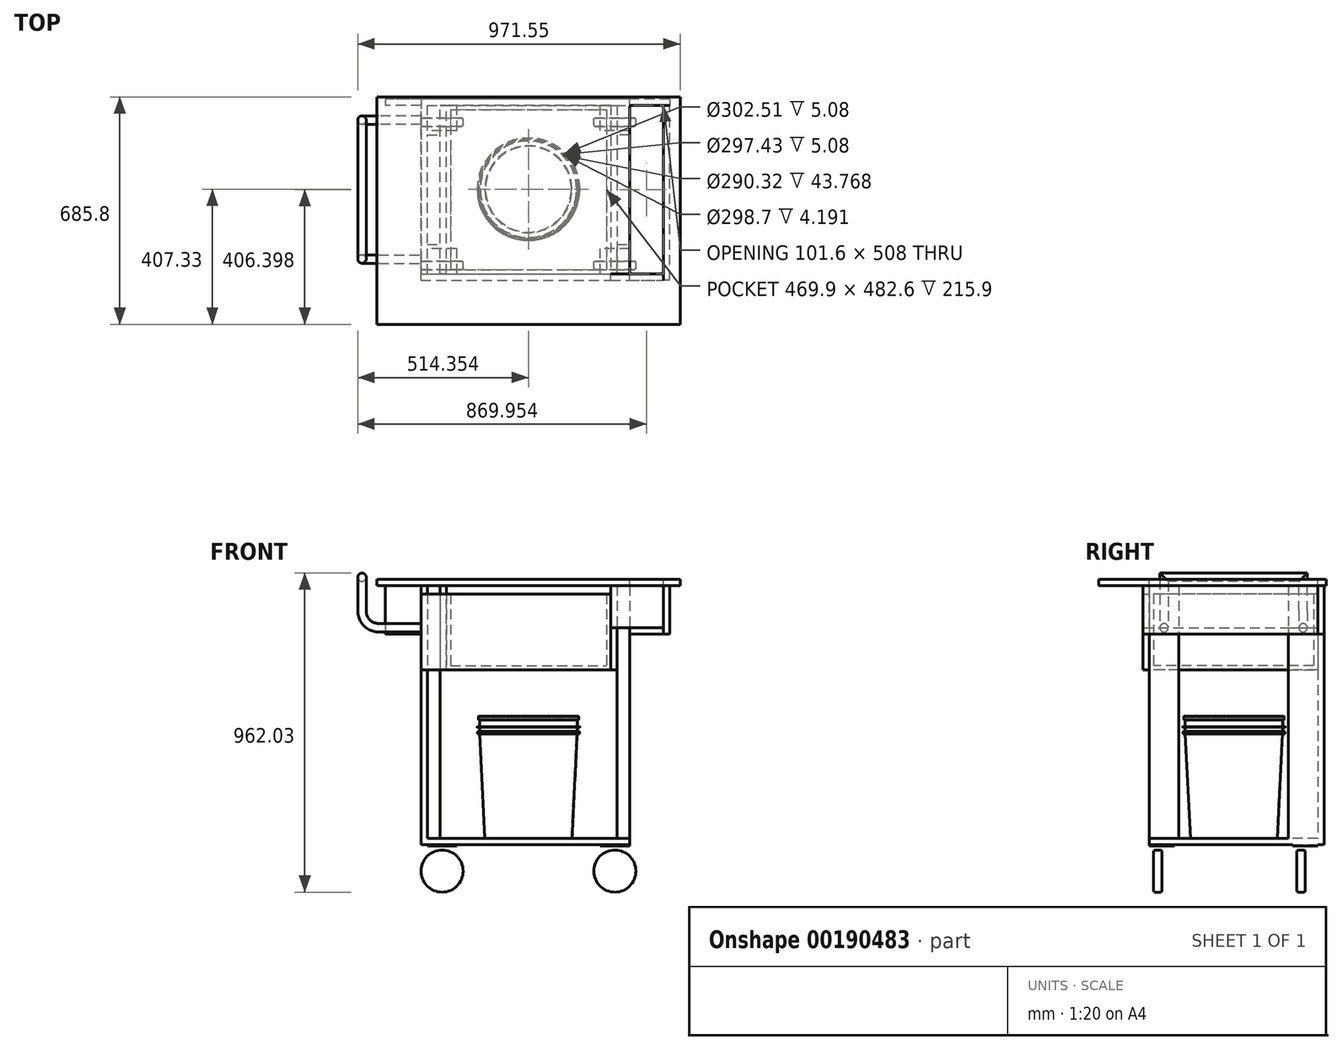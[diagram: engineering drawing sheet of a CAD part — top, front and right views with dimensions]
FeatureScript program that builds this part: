
annotation { "Feature Type Name" : "Feature", "Feature Type Description" : "" }
export const myFeature = defineFeature(function(context is Context, id is Id, definition is map)
    precondition{}
    {
        {
            var Q0;
            Q0=qCreatedBy(makeId("Top.planeOp"),FACE);
            var sketch = newSketch(context, id + "F0", { "sketchPlane" : qUnion([Q0])});
            skLineSegment(sketch, "E0.bottom", {"start": v(-54.98, -51.73) * mm, "end": v(554.62, -51.73) * mm});
            skLineSegment(sketch, "E0.top", {"start": v(-54.98, 456.27) * mm, "end": v(554.62, 456.27) * mm});
            skLineSegment(sketch, "E0.left", {"start": v(-54.98, -51.73) * mm, "end": v(-54.98, 456.27) * mm});
            skLineSegment(sketch, "E0.right", {"start": v(554.62, -51.73) * mm, "end": v(554.62, 456.27) * mm});
            skSolve(sketch);
        }
        {
            var Q0;
            Q0=makeQuery(id+"F0.imprint","IMPRINT",FACE,{"disambiguationData":[TD([[makeQuery(id+"F0.imprint","IMPRINT",EDGE,{"derivedFrom":sQuery(id+"F0.wireOp",EDGE,"E0.bottom")}),1.0]])]});
            var sketch = newSketch(context, id + "F1", { "sketchPlane" : qUnion([Q0])});
            skLineSegment(sketch, "E1.bottom", {"start": v(-54.98, 456.27) * mm, "end": v(-16.88, 456.27) * mm});
            skLineSegment(sketch, "E1.top", {"start": v(-54.98, 367.37) * mm, "end": v(-16.88, 367.37) * mm});
            skLineSegment(sketch, "E1.left", {"start": v(-54.98, 456.27) * mm, "end": v(-54.98, 367.37) * mm});
            skLineSegment(sketch, "E1.right", {"start": v(-16.88, 456.27) * mm, "end": v(-16.88, 367.37) * mm});
            skLineSegment(sketch, "E2.bottom", {"start": v(554.62, 456.27) * mm, "end": v(516.52, 456.27) * mm});
            skLineSegment(sketch, "E2.top", {"start": v(554.62, 367.37) * mm, "end": v(516.52, 367.37) * mm});
            skLineSegment(sketch, "E2.left", {"start": v(554.62, 456.27) * mm, "end": v(554.62, 367.37) * mm});
            skLineSegment(sketch, "E2.right", {"start": v(516.52, 456.27) * mm, "end": v(516.52, 367.37) * mm});
            skLineSegment(sketch, "E3.bottom", {"start": v(516.52, -51.73) * mm, "end": v(554.62, -51.73) * mm});
            skLineSegment(sketch, "E3.top", {"start": v(516.52, 37.17) * mm, "end": v(554.62, 37.17) * mm});
            skLineSegment(sketch, "E3.left", {"start": v(516.52, -51.73) * mm, "end": v(516.52, 37.17) * mm});
            skLineSegment(sketch, "E3.right", {"start": v(554.62, -51.73) * mm, "end": v(554.62, 37.17) * mm});
            skLineSegment(sketch, "E4.bottom", {"start": v(-54.98, -51.73) * mm, "end": v(-16.88, -51.73) * mm});
            skLineSegment(sketch, "E4.top", {"start": v(-54.98, 37.17) * mm, "end": v(-16.88, 37.17) * mm});
            skLineSegment(sketch, "E4.left", {"start": v(-54.98, -51.73) * mm, "end": v(-54.98, 37.17) * mm});
            skLineSegment(sketch, "E4.right", {"start": v(-16.88, -51.73) * mm, "end": v(-16.88, 37.17) * mm});
            skSolve(sketch);
        }
        {
            var Q0;
            Q0=makeQuery(id+"F1.imprint","IMPRINT",FACE,{"disambiguationData":[TD([[makeQuery(id+"F1.imprint","IMPRINT",EDGE,{"derivedFrom":sQuery(id+"F1.wireOp",EDGE,"E1.bottom")}),-1.0]])]});
            var Q1;
            Q1=makeQuery(id+"F1.imprint","IMPRINT",FACE,{"disambiguationData":[TD([[makeQuery(id+"F1.imprint","IMPRINT",EDGE,{"derivedFrom":sQuery(id+"F1.wireOp",EDGE,"E2.bottom")}),-1.0]])]});
            var Q2;
            Q2=makeQuery(id+"F1.imprint","IMPRINT",FACE,{"disambiguationData":[TD([[makeQuery(id+"F1.imprint","IMPRINT",EDGE,{"derivedFrom":sQuery(id+"F1.wireOp",EDGE,"E3.bottom")}),1.0]])]});
            var Q3;
            Q3=makeQuery(id+"F1.imprint","IMPRINT",FACE,{"disambiguationData":[TD([[makeQuery(id+"F1.imprint","IMPRINT",EDGE,{"derivedFrom":sQuery(id+"F1.wireOp",EDGE,"E4.bottom")}),1.0]])]});
            extrude(context, id + "F2", {"entities" : qUnion([Q0, Q1, Q2, Q3]), "depth" : 762 * mm});
        }
        {
            var Q0;
            Q0=makeQuery(id+"F0.imprint","IMPRINT",FACE,{"disambiguationData":[TD([[makeQuery(id+"F0.imprint","IMPRINT",EDGE,{"derivedFrom":sQuery(id+"F0.wireOp",EDGE,"E0.bottom")}),1.0]])]});
            extrude(context, id + "F3", {"entities" : qUnion([Q0]), "oppositeDirection" : true, "depth" : 19.05 * mm});
        }
        {
            var Q0;
            Q0=makeQuery(id+"F2.opExtrude","CAP_FACE",FACE,{"disambiguationData":[OSD([sQuery(id+"F1.wireOp",EDGE,"E1.bottom"),sQuery(id+"F1.wireOp",EDGE,"E1.top"),sQuery(id+"F1.wireOp",EDGE,"E1.left"),sQuery(id+"F1.wireOp",EDGE,"E1.right")])],"isStart":false});
            var sketch = newSketch(context, id + "F4", { "sketchPlane" : qUnion([Q0])});
            skLineSegment(sketch, "E5.bottom", {"start": v(-207.38, 481.67) * mm, "end": v(707.02, 481.67) * mm});
            skLineSegment(sketch, "E5.top", {"start": v(-207.38, -204.13) * mm, "end": v(707.02, -204.13) * mm});
            skLineSegment(sketch, "E5.left", {"start": v(-207.38, 481.67) * mm, "end": v(-207.38, -204.13) * mm});
            skLineSegment(sketch, "E5.right", {"start": v(707.02, 481.67) * mm, "end": v(707.02, -204.13) * mm});
            skSolve(sketch);
        }
        {
            var Q0;
            Q0=makeQuery(id+"F4.imprint","IMPRINT",FACE,{"disambiguationData":[TD([[makeQuery(id+"F4.imprint","IMPRINT",EDGE,{"derivedFrom":sQuery(id+"F4.wireOp",EDGE,"E5.top")}),1.0]])]});
            var Q1;
            Q1=makeQuery(id+"F4.imprint","IMPRINT",FACE,{"disambiguationData":[TD([[makeQuery(id+"F4.imprint","IMPRINT",EDGE,{"derivedFrom":makeQuery(id+"F2.opExtrude","CAP_EDGE",EDGE,{"disambiguationData":[OSD([sQuery(id+"F1.wireOp",EDGE,"E1.top")])],"isStart":false})}),1.0]])]});
            extrude(context, id + "F5", {"entities" : qUnion([Q0, Q1]), "depth" : 19.05 * mm});
        }
        {
            var Q0;
            Q0=qCreatedBy(makeId("Front.planeOp"),FACE);
            cPlane(context, id + "F6", {"entities" : qUnion([Q0]), "cplaneType" : CPlaneType.OFFSET, "offset" : 203.2 * mm, "oppositeDirection" : true, "width" : 152.4 * mm, "height" : 152.4 * mm});
        }
        {
            var Q0;
            Q0=qCreatedBy(id+"F6.planeOp",FACE);
            var sketch = newSketch(context, id + "F7", { "sketchPlane" : qUnion([Q0])});
            skLineSegment(sketch, "E6", {"start": v(249.82, 0) * mm, "end": v(381.02, 0) * mm});
            skLineSegment(sketch, "E7", {"start": v(249.82, 368.3) * mm, "end": v(401.08, 368.3) * mm});
            skLineSegment(sketch, "E8", {"start": v(249.82, 368.3) * mm, "end": v(249.82, 0) * mm});
            skLineSegment(sketch, "E9", {"start": v(401.08, 368.3) * mm, "end": v(401.08, 357.12) * mm});
            skLineSegment(sketch, "E10", {"start": v(401.08, 357.12) * mm, "end": v(398.54, 357.12) * mm});
            skLineSegment(sketch, "E11", {"start": v(398.54, 357.12) * mm, "end": v(398.54, 362.2) * mm});
            skLineSegment(sketch, "E12", {"start": v(398.54, 362.2) * mm, "end": v(396.9, 362.2) * mm});
            skLineSegment(sketch, "E13", {"start": v(396.9, 362.2) * mm, "end": v(396.9, 336.8) * mm});
            skLineSegment(sketch, "E14", {"start": v(396.9, 336.8) * mm, "end": v(404.51, 336.8) * mm});
            skLineSegment(sketch, "E15", {"start": v(404.51, 336.8) * mm, "end": v(404.51, 334.9) * mm});
            skLineSegment(sketch, "E16", {"start": v(404.51, 334.9) * mm, "end": v(396.9, 334.9) * mm});
            skLineSegment(sketch, "E17", {"start": v(396.9, 334.9) * mm, "end": v(396.9, 322.2) * mm});
            skLineSegment(sketch, "E18", {"start": v(396.9, 322.2) * mm, "end": v(403.37, 322.2) * mm});
            skLineSegment(sketch, "E19", {"start": v(403.37, 322.2) * mm, "end": v(403.37, 315.21) * mm});
            skLineSegment(sketch, "E20", {"start": v(403.37, 315.21) * mm, "end": v(401.08, 315.21) * mm});
            skLineSegment(sketch, "E21", {"start": v(401.08, 315.21) * mm, "end": v(401.08, 320.3) * mm});
            skLineSegment(sketch, "E22", {"start": v(401.08, 320.3) * mm, "end": v(396.9, 320.3) * mm});
            skLineSegment(sketch, "E23", {"start": v(396.9, 320.3) * mm, "end": v(381.02, 0) * mm});
            skSolve(sketch);
        }
        {
            var Q0;
            Q0=makeQuery(id+"F7.imprint","IMPRINT",FACE,{"disambiguationData":[TD([[makeQuery(id+"F7.imprint","IMPRINT",EDGE,{"derivedFrom":sQuery(id+"F7.wireOp",EDGE,"E6")}),1.0]])]});
            var Q1;
            Q1=sQuery(id+"F7.wireOp",EDGE,"E8");
            revolve(context, id + "F8", {"entities" : qUnion([Q0]), "axis" : qUnion([Q1]), "revolveType" : RevolveType.FULL});
        }
        {
            var Q0;
            Q0=makeQuery(id+"F8.opRevolve","SWEPT_FACE",FACE,{"disambiguationData":[OSD([sQuery(id+"F7.wireOp",EDGE,"E7")])]});
            shell(context, id + "F9", {"entities" : qUnion([Q0]), "thickness" : 1.9 * mm});
        }
        {
            var Q0;
            Q0=makeQuery(id+"F8.opRevolve","SWEPT_EDGE",EDGE,{"disambiguationData":[OSD([sQuery(id+"F7.wireOp",EDGE,"E18"),sQuery(id+"F7.wireOp",EDGE,"E19")])]});
            var Q1;
            Q1=makeQuery(id+"F8.opRevolve","SWEPT_EDGE",EDGE,{"disambiguationData":[OSD([sQuery(id+"F7.wireOp",EDGE,"E7"),sQuery(id+"F7.wireOp",EDGE,"E9")])]});
            fillet(context, id + "F10", {"entities" : qUnion([Q0, Q1]), "radius" : 1.52 * mm, "tangentPropagation" : true, "allowEdgeOverflow" : false});
        }
        {
            var Q0;
            Q0=makeQuery(id+"F8.opRevolve","SWEPT_EDGE",EDGE,{"disambiguationData":[OSD([sQuery(id+"F7.wireOp",EDGE,"E14"),sQuery(id+"F7.wireOp",EDGE,"E15")])]});
            var Q1;
            Q1=makeQuery(id+"F8.opRevolve","SWEPT_EDGE",EDGE,{"disambiguationData":[OSD([sQuery(id+"F7.wireOp",EDGE,"E15"),sQuery(id+"F7.wireOp",EDGE,"E16")])]});
            fillet(context, id + "F11", {"entities" : qUnion([Q0, Q1]), "radius" : 0.76 * mm, "tangentPropagation" : true, "allowEdgeOverflow" : false});
        }
        {
            var Q0;
            Q0=makeQuery(id+"F2.opExtrude","SWEPT_FACE",FACE,{"disambiguationData":[OSD([sQuery(id+"F1.wireOp",EDGE,"E2.right")])]});
            var sketch = newSketch(context, id + "F12", { "sketchPlane" : qUnion([Q0])});
            skLineSegment(sketch, "E24.bottom", {"start": v(-456.27, 762) * mm, "end": v(51.73, 762) * mm});
            skLineSegment(sketch, "E24.top", {"start": v(-456.27, 508) * mm, "end": v(51.73, 508) * mm});
            skLineSegment(sketch, "E24.left", {"start": v(-456.27, 762) * mm, "end": v(-456.27, 508) * mm});
            skLineSegment(sketch, "E24.right", {"start": v(51.73, 762) * mm, "end": v(51.73, 508) * mm});
            skSolve(sketch);
        }
        {
            var Q0;
            {var subQ3=sQuery(id+"F12.wireOp",EDGE,"E24.right");Q0=makeQuery(id+"F12.imprint","IMPRINT",FACE,{"disambiguationData":[TD([[makeQuery(id+"F12.imprint","IMPRINT",EDGE,{"derivedFrom":subQ3}),-1.0]])]});}
            var Q1;
            {var subQ0=sQuery(id+"F12.wireOp",EDGE,"E24.left");Q1=makeQuery(id+"F12.imprint","IMPRINT",FACE,{"disambiguationData":[TD([[makeQuery(id+"F12.imprint","IMPRINT",EDGE,{"derivedFrom":subQ0}),1.0]])]});}
            extrude(context, id + "F13", {"entities" : qUnion([Q0, Q1]), "depth" : 19.05 * mm});
        }
        {
            var Q0;
            Q0=makeQuery(id+"F2.opExtrude","SWEPT_FACE",FACE,{"disambiguationData":[OSD([sQuery(id+"F1.wireOp",EDGE,"E3.bottom")])]});
            var sketch = newSketch(context, id + "F14", { "sketchPlane" : qUnion([Q0])});
            skLineSegment(sketch, "E25.bottom", {"start": v(497.47, 635) * mm, "end": v(656.22, 635) * mm});
            skLineSegment(sketch, "E25.top", {"start": v(497.47, 762) * mm, "end": v(656.22, 762) * mm});
            skLineSegment(sketch, "E25.left", {"start": v(497.47, 635) * mm, "end": v(497.47, 762) * mm});
            skLineSegment(sketch, "E25.right", {"start": v(656.22, 635) * mm, "end": v(656.22, 762) * mm});
            skSolve(sketch);
        }
        {
            var Q0;
            {var subQ0=sQuery(id+"F14.wireOp",EDGE,"E25.right");Q0=makeQuery(id+"F14.imprint","IMPRINT",FACE,{"disambiguationData":[TD([[makeQuery(id+"F14.imprint","IMPRINT",EDGE,{"derivedFrom":subQ0}),1.0]])]});}
            var Q1;
            {var subQ0=sQuery(id+"F14.wireOp",EDGE,"E25.bottom");var subQ1=sQuery(id+"F1.wireOp",EDGE,"E3.bottom");var subQ4=makeQuery(id+"F2.opExtrude","SWEPT_EDGE",EDGE,{"disambiguationData":[OSD([subQ1,sQuery(id+"F1.wireOp",EDGE,"E3.right")])]});var subQ5=makeQuery(id+"F14.imprint","INTERSECT",VERTEX,{"derivedFrom":[subQ4,subQ0]});Q1=makeQuery(id+"F14.imprint","IMPRINT",FACE,{"disambiguationData":[TD([[makeQuery(id+"F14.imprint","IMPRINT",EDGE,{"disambiguationData":[TD([[subQ5,1.0]])],"derivedFrom":subQ0}),1.0]])]});}
            var Q2;
            {var subQ0=sQuery(id+"F14.wireOp",EDGE,"E25.left");Q2=makeQuery(id+"F14.imprint","IMPRINT",FACE,{"disambiguationData":[TD([[makeQuery(id+"F14.imprint","IMPRINT",EDGE,{"derivedFrom":subQ0}),-1.0]])]});}
            extrude(context, id + "F15", {"entities" : qUnion([Q0, Q1, Q2]), "depth" : 19.05 * mm});
        }
        {
            var Q0;
            Q0=makeQuery(id+"F2.opExtrude","SWEPT_FACE",FACE,{"disambiguationData":[OSD([sQuery(id+"F1.wireOp",EDGE,"E2.bottom")])]});
            var sketch = newSketch(context, id + "F16", { "sketchPlane" : qUnion([Q0])});
            skLineSegment(sketch, "E26.bottom", {"start": v(-497.47, 762) * mm, "end": v(-656.22, 762) * mm});
            skLineSegment(sketch, "E26.top", {"start": v(-497.47, 635) * mm, "end": v(-656.22, 635) * mm});
            skLineSegment(sketch, "E26.left", {"start": v(-497.47, 762) * mm, "end": v(-497.47, 635) * mm});
            skLineSegment(sketch, "E26.right", {"start": v(-656.22, 762) * mm, "end": v(-656.22, 635) * mm});
            skSolve(sketch);
        }
        {
            var Q0;
            {var subQ3=sQuery(id+"F16.wireOp",EDGE,"E26.left");Q0=makeQuery(id+"F16.imprint","IMPRINT",FACE,{"disambiguationData":[TD([[makeQuery(id+"F16.imprint","IMPRINT",EDGE,{"derivedFrom":subQ3}),-1.0]])]});}
            var Q1;
            {var subQ0=sQuery(id+"F16.wireOp",EDGE,"E26.bottom");var subQ1=sQuery(id+"F1.wireOp",EDGE,"E2.bottom");var subQ2=makeQuery(id+"F2.opExtrude","SWEPT_EDGE",EDGE,{"disambiguationData":[OSD([subQ1,sQuery(id+"F1.wireOp",EDGE,"E2.left")])]});var subQ3=makeQuery(id+"F16.imprint","INTERSECT",VERTEX,{"derivedFrom":[subQ2,subQ0]});Q1=makeQuery(id+"F16.imprint","IMPRINT",FACE,{"disambiguationData":[TD([[makeQuery(id+"F16.imprint","IMPRINT",EDGE,{"disambiguationData":[TD([[subQ3,1.0]])],"derivedFrom":subQ0}),1.0]])]});}
            var Q2;
            {var subQ3=sQuery(id+"F16.wireOp",EDGE,"E26.right");Q2=makeQuery(id+"F16.imprint","IMPRINT",FACE,{"disambiguationData":[TD([[makeQuery(id+"F16.imprint","IMPRINT",EDGE,{"derivedFrom":subQ3}),1.0]])]});}
            extrude(context, id + "F17", {"entities" : qUnion([Q0, Q1, Q2]), "depth" : 19.05 * mm});
        }
        {
            var Q0;
            Q0=makeQuery(id+"F15.opExtrude","SWEPT_FACE",FACE,{"disambiguationData":[OSD([sQuery(id+"F14.wireOp",EDGE,"E25.bottom")])]});
            var sketch = newSketch(context, id + "F18", { "sketchPlane" : qUnion([Q0])});
            skLineSegment(sketch, "E27.bottom", {"start": v(656.22, 70.78) * mm, "end": v(554.62, 70.78) * mm});
            skLineSegment(sketch, "E27.top", {"start": v(656.22, -456.27) * mm, "end": v(554.62, -456.27) * mm});
            skLineSegment(sketch, "E27.left", {"start": v(656.22, 70.78) * mm, "end": v(656.22, -456.27) * mm});
            skLineSegment(sketch, "E27.right", {"start": v(554.62, 70.78) * mm, "end": v(554.62, -456.27) * mm});
            skSolve(sketch);
        }
        {
            var Q0;
            {var subQ0=sQuery(id+"F18.wireOp",EDGE,"E27.bottom");Q0=makeQuery(id+"F18.imprint","IMPRINT",FACE,{"disambiguationData":[TD([[makeQuery(id+"F18.imprint","IMPRINT",EDGE,{"derivedFrom":subQ0}),-1.0]])]});}
            var Q1;
            {var subQ0=sQuery(id+"F18.wireOp",EDGE,"E27.top");Q1=makeQuery(id+"F18.imprint","IMPRINT",FACE,{"disambiguationData":[TD([[makeQuery(id+"F18.imprint","IMPRINT",EDGE,{"derivedFrom":subQ0}),-1.0]])]});}
            extrude(context, id + "F19", {"entities" : qUnion([Q0, Q1]), "depth" : 19.05 * mm});
        }
        {
            var Q0;
            Q0=makeQuery(id+"F15.opExtrude","SWEPT_FACE",FACE,{"disambiguationData":[OSD([sQuery(id+"F14.wireOp",EDGE,"E25.right")])]});
            var sketch = newSketch(context, id + "F20", { "sketchPlane" : qUnion([Q0])});
            skLineSegment(sketch, "E28.bottom", {"start": v(-70.78, 615.95) * mm, "end": v(456.27, 615.95) * mm});
            skLineSegment(sketch, "E28.top", {"start": v(-70.78, 762) * mm, "end": v(456.27, 762) * mm});
            skLineSegment(sketch, "E28.left", {"start": v(-70.78, 615.95) * mm, "end": v(-70.78, 762) * mm});
            skLineSegment(sketch, "E28.right", {"start": v(456.27, 615.95) * mm, "end": v(456.27, 762) * mm});
            skSolve(sketch);
        }
        {
            var Q0;
            {var subQ3=sQuery(id+"F20.wireOp",EDGE,"E28.bottom");Q0=makeQuery(id+"F20.imprint","IMPRINT",FACE,{"disambiguationData":[TD([[makeQuery(id+"F20.imprint","IMPRINT",EDGE,{"derivedFrom":subQ3}),1.0]])]});}
            var Q1;
            {var subQ1=sQuery(id+"F14.wireOp",EDGE,"E25.right");var subQ2=makeQuery(id+"F15.opExtrude","CAP_EDGE",EDGE,{"disambiguationData":[OSD([subQ1])],"isStart":true});Q1=makeQuery(id+"F20.imprint","IMPRINT",FACE,{"disambiguationData":[TD([[makeQuery(id+"F20.imprint","IMPRINT",EDGE,{"derivedFrom":subQ2}),1.0]])]});}
            extrude(context, id + "F21", {"entities" : qUnion([Q0, Q1]), "depth" : 19.05 * mm});
        }
        {
            var Q0;
            Q0=makeQuery(id+"F5.opExtrude","CAP_FACE",FACE,{"disambiguationData":[OSD([sQuery(id+"F4.wireOp",EDGE,"E5.bottom"),sQuery(id+"F4.wireOp",EDGE,"E5.top"),sQuery(id+"F4.wireOp",EDGE,"E5.left"),sQuery(id+"F4.wireOp",EDGE,"E5.right")])],"isStart":false});
            var sketch = newSketch(context, id + "F22", { "sketchPlane" : qUnion([Q0])});
            skLineSegment(sketch, "E29.bottom", {"start": v(554.62, -51.73) * mm, "end": v(656.22, -51.73) * mm});
            skLineSegment(sketch, "E29.top", {"start": v(554.62, 456.27) * mm, "end": v(656.22, 456.27) * mm});
            skLineSegment(sketch, "E29.left", {"start": v(554.62, -51.73) * mm, "end": v(554.62, 456.27) * mm});
            skLineSegment(sketch, "E29.right", {"start": v(656.22, -51.73) * mm, "end": v(656.22, 456.27) * mm});
            skSolve(sketch);
        }
        {
            var Q0;
            Q0=makeQuery(id+"F22.imprint","IMPRINT",FACE,{"disambiguationData":[TD([[makeQuery(id+"F22.imprint","IMPRINT",EDGE,{"derivedFrom":sQuery(id+"F22.wireOp",EDGE,"E29.bottom")}),1.0]])]});
            extrude(context, id + "F23", {"entities" : qUnion([Q0]), "operationType" : NewBodyOperationType.REMOVE, "oppositeDirection" : true, "depth" : 25.4 * mm});
        }
        {
            var Q0;
            Q0=makeQuery(id+"F2.opExtrude","SWEPT_FACE",FACE,{"disambiguationData":[OSD([sQuery(id+"F1.wireOp",EDGE,"E1.left")])]});
            var sketch = newSketch(context, id + "F24", { "sketchPlane" : qUnion([Q0])});
            skLineSegment(sketch, "E30.bottom", {"start": v(-456.27, 762) * mm, "end": v(51.73, 762) * mm});
            skLineSegment(sketch, "E30.top", {"start": v(-456.27, -19.05) * mm, "end": v(51.73, -19.05) * mm});
            skLineSegment(sketch, "E30.left", {"start": v(-456.27, 762) * mm, "end": v(-456.27, -19.05) * mm});
            skLineSegment(sketch, "E30.right", {"start": v(51.73, 762) * mm, "end": v(51.73, -19.05) * mm});
            skSolve(sketch);
        }
        {
            var Q0;
            {var subQ3=sQuery(id+"F1.wireOp",EDGE,"E1.left");var subQ5=makeQuery(id+"F2.opExtrude","CAP_EDGE",EDGE,{"disambiguationData":[OSD([subQ3])],"isStart":true});Q0=makeQuery(id+"F24.imprint","IMPRINT",FACE,{"disambiguationData":[TD([[makeQuery(id+"F24.imprint","IMPRINT",EDGE,{"derivedFrom":subQ5}),-1.0]])]});}
            var Q1;
            {var subQ4=sQuery(id+"F24.wireOp",EDGE,"E30.top");Q1=makeQuery(id+"F24.imprint","IMPRINT",FACE,{"disambiguationData":[TD([[makeQuery(id+"F24.imprint","IMPRINT",EDGE,{"derivedFrom":subQ4}),1.0]])]});}
            extrude(context, id + "F25", {"entities" : qUnion([Q0, Q1]), "depth" : 19.05 * mm});
        }
        {
            var Q0;
            Q0=makeQuery(id+"F3.opExtrude","CAP_FACE",FACE,{"disambiguationData":[OSD([sQuery(id+"F0.wireOp",EDGE,"E0.bottom"),sQuery(id+"F0.wireOp",EDGE,"E0.top"),sQuery(id+"F0.wireOp",EDGE,"E0.left"),sQuery(id+"F0.wireOp",EDGE,"E0.right")])],"isStart":false});
            var sketch = newSketch(context, id + "F26", { "sketchPlane" : qUnion([Q0])});
            skLineSegment(sketch, "E31.bottom", {"start": v(554.62, 51.73) * mm, "end": v(465.72, 51.73) * mm});
            skLineSegment(sketch, "E31.top", {"start": v(554.62, -24.47) * mm, "end": v(465.72, -24.47) * mm});
            skLineSegment(sketch, "E31.left", {"start": v(554.62, 51.73) * mm, "end": v(554.62, -24.47) * mm});
            skLineSegment(sketch, "E31.right", {"start": v(465.72, 51.73) * mm, "end": v(465.72, -24.47) * mm});
            skLineSegment(sketch, "E32.0.1.0", {"start": v(554.62, -380.07) * mm, "end": v(554.62, -456.27) * mm});
            skLineSegment(sketch, "E32.0.1.1", {"start": v(554.62, -456.27) * mm, "end": v(465.72, -456.27) * mm});
            skLineSegment(sketch, "E32.0.1.2", {"start": v(465.72, -380.07) * mm, "end": v(465.72, -456.27) * mm});
            skLineSegment(sketch, "E32.0.1.3", {"start": v(554.62, -380.07) * mm, "end": v(465.72, -380.07) * mm});
            skLineSegment(sketch, "E32.1.0.0", {"start": v(33.92, 51.73) * mm, "end": v(33.92, -24.47) * mm});
            skLineSegment(sketch, "E32.1.0.1", {"start": v(33.92, -24.47) * mm, "end": v(-54.98, -24.47) * mm});
            skLineSegment(sketch, "E32.1.0.2", {"start": v(-54.98, 51.73) * mm, "end": v(-54.98, -24.47) * mm});
            skLineSegment(sketch, "E32.1.0.3", {"start": v(33.92, 51.73) * mm, "end": v(-54.98, 51.73) * mm});
            skLineSegment(sketch, "E32.1.1.0", {"start": v(33.92, -380.07) * mm, "end": v(33.92, -456.27) * mm});
            skLineSegment(sketch, "E32.1.1.1", {"start": v(33.92, -456.27) * mm, "end": v(-54.98, -456.27) * mm});
            skLineSegment(sketch, "E32.1.1.2", {"start": v(-54.98, -380.07) * mm, "end": v(-54.98, -456.27) * mm});
            skLineSegment(sketch, "E32.1.1.3", {"start": v(33.92, -380.07) * mm, "end": v(-54.98, -380.07) * mm});
            skLineSegment(sketch, "E32.direction1", {"start": v(554.62, -24.47) * mm, "end": v(33.92, -24.47) * mm, "construction": true});
            skLineSegment(sketch, "E32.direction2", {"start": v(554.62, -24.47) * mm, "end": v(554.62, -456.27) * mm, "construction": true});
            skSolve(sketch);
        }
        {
            var Q0;
            Q0=makeQuery(id+"F26.imprint","IMPRINT",FACE,{"disambiguationData":[TD([[makeQuery(id+"F26.imprint","IMPRINT",EDGE,{"derivedFrom":sQuery(id+"F26.wireOp",EDGE,"E31.bottom")}),-1.0]])]});
            var Q1;
            Q1=makeQuery(id+"F26.imprint","IMPRINT",FACE,{"disambiguationData":[TD([[makeQuery(id+"F26.imprint","IMPRINT",EDGE,{"derivedFrom":sQuery(id+"F26.wireOp",EDGE,"E32.0.1.0")}),-1.0]])]});
            var Q2;
            Q2=makeQuery(id+"F26.imprint","IMPRINT",FACE,{"disambiguationData":[TD([[makeQuery(id+"F26.imprint","IMPRINT",EDGE,{"derivedFrom":sQuery(id+"F26.wireOp",EDGE,"E32.1.1.0")}),-1.0]])]});
            var Q3;
            Q3=makeQuery(id+"F26.imprint","IMPRINT",FACE,{"disambiguationData":[TD([[makeQuery(id+"F26.imprint","IMPRINT",EDGE,{"derivedFrom":sQuery(id+"F26.wireOp",EDGE,"E32.1.0.0")}),-1.0]])]});
            extrude(context, id + "F27", {"entities" : qUnion([Q0, Q1, Q2, Q3]), "depth" : 3.17 * mm});
        }
        {
            var Q0;
            Q0=makeQuery(id+"F3.opExtrude","SWEPT_FACE",FACE,{"disambiguationData":[OSD([sQuery(id+"F0.wireOp",EDGE,"E0.bottom")])]});
            cPlane(context, id + "F28", {"entities" : qUnion([Q0]), "cplaneType" : CPlaneType.OFFSET, "offset" : 38.1 * mm, "oppositeDirection" : true, "width" : 152.4 * mm, "height" : 152.4 * mm});
        }
        {
            var Q0;
            Q0=qCreatedBy(id+"F28.planeOp",FACE);
            var sketch = newSketch(context, id + "F29", { "sketchPlane" : qUnion([Q0])});
            skCircle(sketch, "E33", {"center": v(510.17, -98.43) * mm, "radius": 63.5 * mm});
            skCircle(sketch, "E34.1.0.0", {"center": v(-10.53, -98.43) * mm, "radius": 63.5 * mm});
            skLineSegment(sketch, "E34.direction1", {"start": v(510.17, -98.43) * mm, "end": v(-10.53, -98.43) * mm, "construction": true});
            skSolve(sketch);
        }
        {
            var Q0;
            Q0=makeQuery(id+"F2.opExtrude","SWEPT_FACE",FACE,{"disambiguationData":[OSD([sQuery(id+"F1.wireOp",EDGE,"E2.bottom")])]});
            cPlane(context, id + "F30", {"entities" : qUnion([Q0]), "cplaneType" : CPlaneType.OFFSET, "offset" : 38.1 * mm, "oppositeDirection" : true, "width" : 152.4 * mm, "height" : 152.4 * mm});
        }
        {
            var Q0;
            Q0=qCreatedBy(id+"F30.planeOp",FACE);
            var sketch = newSketch(context, id + "F31", { "sketchPlane" : qUnion([Q0])});
            skCircle(sketch, "E35", {"center": v(-510.17, -98.43) * mm, "radius": 63.5 * mm});
            skCircle(sketch, "E36", {"center": v(10.53, -98.42) * mm, "radius": 63.5 * mm});
            skSolve(sketch);
        }
        {
            var Q0;
            Q0=makeQuery(id+"F29.imprint","IMPRINT",FACE,{"disambiguationData":[TD([[makeQuery(id+"F29.imprint","IMPRINT",EDGE,{"derivedFrom":sQuery(id+"F29.wireOp",EDGE,"E33")}),1.0]])]});
            var Q1;
            Q1=makeQuery(id+"F31.imprint","IMPRINT",FACE,{"disambiguationData":[TD([[makeQuery(id+"F31.imprint","IMPRINT",EDGE,{"derivedFrom":sQuery(id+"F31.wireOp",EDGE,"E35")}),1.0]])]});
            var Q2;
            Q2=makeQuery(id+"F29.imprint","IMPRINT",FACE,{"disambiguationData":[TD([[makeQuery(id+"F29.imprint","IMPRINT",EDGE,{"derivedFrom":sQuery(id+"F29.wireOp",EDGE,"E34.1.0.0")}),1.0]])]});
            var Q3;
            Q3=makeQuery(id+"F31.imprint","IMPRINT",FACE,{"disambiguationData":[TD([[makeQuery(id+"F31.imprint","IMPRINT",EDGE,{"derivedFrom":sQuery(id+"F31.wireOp",EDGE,"E36")}),1.0]])]});
            extrude(context, id + "F32", {"entities" : qUnion([Q0, Q1, Q2, Q3]), "depth" : 25.4 * mm});
        }
        {
            var Q0;
            Q0=makeQuery(id+"F32.opExtrude","CAP_EDGE",EDGE,{"disambiguationData":[OSD([sQuery(id+"F29.wireOp",EDGE,"E34.1.0.0")])],"isStart":true});
            var Q1;
            Q1=makeQuery(id+"F32.opExtrude","CAP_EDGE",EDGE,{"disambiguationData":[OSD([sQuery(id+"F29.wireOp",EDGE,"E34.1.0.0")])],"isStart":false});
            var Q2;
            Q2=makeQuery(id+"F32.opExtrude","CAP_EDGE",EDGE,{"disambiguationData":[OSD([sQuery(id+"F31.wireOp",EDGE,"E36")])],"isStart":false});
            var Q3;
            Q3=makeQuery(id+"F32.opExtrude","CAP_EDGE",EDGE,{"disambiguationData":[OSD([sQuery(id+"F31.wireOp",EDGE,"E36")])],"isStart":true});
            var Q4;
            Q4=makeQuery(id+"F32.opExtrude","CAP_EDGE",EDGE,{"disambiguationData":[OSD([sQuery(id+"F29.wireOp",EDGE,"E33")])],"isStart":false});
            var Q5;
            Q5=makeQuery(id+"F32.opExtrude","CAP_EDGE",EDGE,{"disambiguationData":[OSD([sQuery(id+"F29.wireOp",EDGE,"E33")])],"isStart":true});
            var Q6;
            Q6=makeQuery(id+"F32.opExtrude","CAP_EDGE",EDGE,{"disambiguationData":[OSD([sQuery(id+"F31.wireOp",EDGE,"E35")])],"isStart":false});
            var Q7;
            Q7=makeQuery(id+"F32.opExtrude","CAP_EDGE",EDGE,{"disambiguationData":[OSD([sQuery(id+"F31.wireOp",EDGE,"E35")])],"isStart":true});
            fillet(context, id + "F33", {"entities" : qUnion([Q0, Q1, Q2, Q3, Q4, Q5, Q6, Q7]), "radius" : 5.08 * mm, "tangentPropagation" : true, "allowEdgeOverflow" : false});
        }
        {
            var Q0;
            Q0=makeQuery(id+"F2.opExtrude","SWEPT_FACE",FACE,{"disambiguationData":[OSD([sQuery(id+"F1.wireOp",EDGE,"E4.right")])]});
            var sketch = newSketch(context, id + "F34", { "sketchPlane" : qUnion([Q0])});
            skLineSegment(sketch, "E37.bottom", {"start": v(-51.73, 508) * mm, "end": v(456.27, 508) * mm});
            skLineSegment(sketch, "E37.top", {"start": v(-51.73, 762) * mm, "end": v(456.27, 762) * mm});
            skLineSegment(sketch, "E37.left", {"start": v(-51.73, 508) * mm, "end": v(-51.73, 762) * mm});
            skLineSegment(sketch, "E37.right", {"start": v(456.27, 508) * mm, "end": v(456.27, 762) * mm});
            skSolve(sketch);
        }
        {
            var Q0;
            {var subQ0=sQuery(id+"F34.wireOp",EDGE,"E37.left");Q0=makeQuery(id+"F34.imprint","IMPRINT",FACE,{"disambiguationData":[TD([[makeQuery(id+"F34.imprint","IMPRINT",EDGE,{"derivedFrom":subQ0}),1.0]])]});}
            var Q1;
            {var subQ0=sQuery(id+"F34.wireOp",EDGE,"E37.right");Q1=makeQuery(id+"F34.imprint","IMPRINT",FACE,{"disambiguationData":[TD([[makeQuery(id+"F34.imprint","IMPRINT",EDGE,{"derivedFrom":subQ0}),1.0]])]});}
            extrude(context, id + "F35", {"entities" : qUnion([Q0, Q1]), "depth" : 19.05 * mm});
        }
        {
            var Q0;
            Q0=makeQuery(id+"F17.opExtrude","SWEPT_BODY",BODY,{"disambiguationData":[OSD([sQuery(id+"F16.wireOp",EDGE,"E26.bottom"),sQuery(id+"F16.wireOp",EDGE,"E26.top"),sQuery(id+"F16.wireOp",EDGE,"E26.left"),sQuery(id+"F16.wireOp",EDGE,"E26.right")])]});
            deleteBodies(context, id + "F36", {"entities" : qUnion([Q0])});
        }
        {
            var Q0;
            Q0=makeQuery(id+"F2.opExtrude","SWEPT_FACE",FACE,{"disambiguationData":[OSD([sQuery(id+"F1.wireOp",EDGE,"E2.bottom")])]});
            var sketch = newSketch(context, id + "F37", { "sketchPlane" : qUnion([Q0])});
            skLineSegment(sketch, "E38.bottom", {"start": v(-675.27, 762) * mm, "end": v(181.98, 762) * mm});
            skLineSegment(sketch, "E38.top", {"start": v(-675.27, 615.95) * mm, "end": v(181.98, 615.95) * mm});
            skLineSegment(sketch, "E38.left", {"start": v(-675.27, 762) * mm, "end": v(-675.27, 615.95) * mm});
            skLineSegment(sketch, "E38.right", {"start": v(181.98, 762) * mm, "end": v(181.98, 615.95) * mm});
            skSolve(sketch);
        }
        {
            var Q0;
            {var subQ1=sQuery(id+"F1.wireOp",EDGE,"E2.bottom");var subQ6=makeQuery(id+"F2.opExtrude","CAP_EDGE",EDGE,{"disambiguationData":[OSD([subQ1])],"isStart":true});Q0=makeQuery(id+"F37.imprint","IMPRINT",FACE,{"disambiguationData":[TD([[makeQuery(id+"F37.imprint","IMPRINT",EDGE,{"derivedFrom":subQ6}),-1.0]])]});}
            var sketch = newSketch(context, id + "F38", { "sketchPlane" : qUnion([Q0])});
            skLineSegment(sketch, "E39.bottom", {"start": v(-554.62, 615.95) * mm, "end": v(74.03, 615.95) * mm});
            skLineSegment(sketch, "E39.top", {"start": v(-554.62, -19.05) * mm, "end": v(74.03, -19.05) * mm});
            skLineSegment(sketch, "E39.left", {"start": v(-554.62, 615.95) * mm, "end": v(-554.62, -19.05) * mm});
            skLineSegment(sketch, "E39.right", {"start": v(74.03, 615.95) * mm, "end": v(74.03, -19.05) * mm});
            skSolve(sketch);
        }
        {
            var Q0;
            {var subQ3=sQuery(id+"F37.wireOp",EDGE,"E38.right");Q0=makeQuery(id+"F37.imprint","IMPRINT",FACE,{"disambiguationData":[TD([[makeQuery(id+"F37.imprint","IMPRINT",EDGE,{"derivedFrom":subQ3}),-1.0]])]});}
            var Q1;
            {var subQ0=sQuery(id+"F37.wireOp",EDGE,"E38.bottom");var subQ1=sQuery(id+"F1.wireOp",EDGE,"E2.bottom");var subQ2=makeQuery(id+"F2.opExtrude","SWEPT_EDGE",EDGE,{"disambiguationData":[OSD([subQ1,sQuery(id+"F1.wireOp",EDGE,"E2.left")])]});var subQ3=makeQuery(id+"F37.imprint","INTERSECT",VERTEX,{"derivedFrom":[subQ2,subQ0]});var subQ4=makeQuery(id+"F2.opExtrude","SWEPT_EDGE",EDGE,{"disambiguationData":[OSD([sQuery(id+"F0.wireOp",EDGE,"E0.top"),subQ1,sQuery(id+"F1.wireOp",EDGE,"E2.right")])]});var subQ5=makeQuery(id+"F37.imprint","INTERSECT",VERTEX,{"derivedFrom":[subQ4,subQ0]});Q1=makeQuery(id+"F37.imprint","IMPRINT",FACE,{"disambiguationData":[TD([[makeQuery(id+"F37.imprint","IMPRINT",EDGE,{"disambiguationData":[TD([[subQ3,1.0],[subQ5,-1.0]])],"derivedFrom":subQ0}),1.0]])]});}
            var Q2;
            {var subQ3=sQuery(id+"F37.wireOp",EDGE,"E38.left");Q2=makeQuery(id+"F37.imprint","IMPRINT",FACE,{"disambiguationData":[TD([[makeQuery(id+"F37.imprint","IMPRINT",EDGE,{"derivedFrom":subQ3}),1.0]])]});}
            extrude(context, id + "F39", {"entities" : qUnion([Q0, Q1, Q2]), "depth" : 19.05 * mm});
        }
        {
            var Q0;
            {var subQ3=sQuery(id+"F1.wireOp",EDGE,"E2.bottom");var subQ4=makeQuery(id+"F2.opExtrude","CAP_EDGE",EDGE,{"disambiguationData":[OSD([subQ3])],"isStart":true});var subQ7=makeQuery(id+"F37.imprint","IMPRINT",EDGE,{"derivedFrom":subQ4});Q0=makeQuery(id+"F38.imprint","IMPRINT",FACE,{"disambiguationData":[TD([[makeQuery(id+"F38.imprint","IMPRINT",EDGE,{"derivedFrom":subQ7}),-1.0]])]});}
            var Q1;
            {var subQ4=sQuery(id+"F38.wireOp",EDGE,"E39.top");Q1=makeQuery(id+"F38.imprint","IMPRINT",FACE,{"disambiguationData":[TD([[makeQuery(id+"F38.imprint","IMPRINT",EDGE,{"derivedFrom":subQ4}),1.0]])]});}
            extrude(context, id + "F40", {"entities" : qUnion([Q0, Q1]), "operationType" : NewBodyOperationType.ADD, "depth" : 19.05 * mm});
        }
        {
            var Q0;
            Q0=makeQuery(id+"F23.boolean.opBoolean","COPY",EDGE,{"derivedFrom":makeQuery(id+"F23.opExtrude","SWEPT_EDGE",EDGE,{"disambiguationData":[OSD([sQuery(id+"F22.wireOp",EDGE,"E29.bottom"),sQuery(id+"F22.wireOp",EDGE,"E29.left")])]})});
            var Q1;
            Q1=makeQuery(id+"F23.boolean.opBoolean","COPY",EDGE,{"derivedFrom":makeQuery(id+"F23.opExtrude","SWEPT_EDGE",EDGE,{"disambiguationData":[OSD([sQuery(id+"F22.wireOp",EDGE,"E29.bottom"),sQuery(id+"F22.wireOp",EDGE,"E29.right")])]})});
            var Q2;
            Q2=makeQuery(id+"F23.boolean.opBoolean","COPY",EDGE,{"derivedFrom":makeQuery(id+"F23.opExtrude","SWEPT_EDGE",EDGE,{"disambiguationData":[OSD([sQuery(id+"F22.wireOp",EDGE,"E29.top"),sQuery(id+"F22.wireOp",EDGE,"E29.right")])]})});
            var Q3;
            Q3=makeQuery(id+"F23.boolean.opBoolean","COPY",EDGE,{"derivedFrom":makeQuery(id+"F23.opExtrude","SWEPT_EDGE",EDGE,{"disambiguationData":[OSD([sQuery(id+"F22.wireOp",EDGE,"E29.top"),sQuery(id+"F22.wireOp",EDGE,"E29.left")])]})});
            fillet(context, id + "F41", {"entities" : qUnion([Q0, Q1, Q2, Q3]), "radius" : 6.35 * mm, "tangentPropagation" : true, "allowEdgeOverflow" : false});
        }
        {
            var Q0;
            Q0=makeQuery(id+"F2.opExtrude","SWEPT_FACE",FACE,{"disambiguationData":[OSD([sQuery(id+"F1.wireOp",EDGE,"E4.bottom")])]});
            cPlane(context, id + "F42", {"entities" : qUnion([Q0]), "cplaneType" : CPlaneType.OFFSET, "offset" : 44.45 * mm, "oppositeDirection" : true, "width" : 152.4 * mm, "height" : 152.4 * mm});
        }
        {
            var Q0;
            Q0=qCreatedBy(id+"F42.planeOp",FACE);
            var sketch = newSketch(context, id + "F43", { "sketchPlane" : qUnion([Q0])});
            skLineSegment(sketch, "E40", {"start": v(-74.03, 635) * mm, "end": v(-201.03, 635) * mm});
            skLineSegment(sketch, "E41", {"start": v(-251.83, 685.8) * mm, "end": v(-251.83, 787.4) * mm});
            skPoint(sketch, "E42.visualSharp", {"position": v(-251.83, 635) * mm});
            skArc(sketch, "E42.filletArc", {"start": v(-251.83, 685.8) * mm, "mid": v(-236.95, 649.88) * mm, "end": v(-201.03, 635) * mm});
            skSolve(sketch);
        }
        {
            var Q0;
            Q0=makeQuery(id+"F40.boolean.opBoolean","MERGE",FACE,{"derivedFrom":[makeQuery(id+"F39.opExtrude","CAP_FACE",FACE,{"disambiguationData":[OSD([sQuery(id+"F37.wireOp",EDGE,"E38.bottom"),sQuery(id+"F37.wireOp",EDGE,"E38.top"),sQuery(id+"F37.wireOp",EDGE,"E38.left"),sQuery(id+"F37.wireOp",EDGE,"E38.right")])],"isStart":false}),makeQuery(id+"F40.opExtrude","CAP_FACE",FACE,{"disambiguationData":[OSD([sQuery(id+"F38.wireOp",EDGE,"E39.bottom"),sQuery(id+"F38.wireOp",EDGE,"E39.top"),sQuery(id+"F38.wireOp",EDGE,"E39.left"),sQuery(id+"F38.wireOp",EDGE,"E39.right")])],"isStart":false})]});
            cPlane(context, id + "F44", {"entities" : qUnion([Q0]), "cplaneType" : CPlaneType.OFFSET, "offset" : 63.5 * mm, "oppositeDirection" : true, "width" : 152.4 * mm, "height" : 152.4 * mm});
        }
        {
            var Q0;
            Q0=qCreatedBy(id+"F44.planeOp",FACE);
            var sketch = newSketch(context, id + "F45", { "sketchPlane" : qUnion([Q0])});
            skLineSegment(sketch, "E43", {"start": v(74.03, 635) * mm, "end": v(201.03, 635) * mm});
            skLineSegment(sketch, "E44", {"start": v(251.83, 685.8) * mm, "end": v(251.83, 787.4) * mm});
            skPoint(sketch, "E45.visualSharp", {"position": v(251.83, 635) * mm});
            skArc(sketch, "E45.filletArc", {"start": v(201.03, 635) * mm, "mid": v(236.95, 649.88) * mm, "end": v(251.83, 685.8) * mm});
            skSolve(sketch);
        }
        {
            var Q0;
            Q0=sQuery(id+"F45.wireOp",VERTEX,"E44.end");
            var Q1;
            Q1=sQuery(id+"F45.wireOp",VERTEX,"E45.filletArc.end");
            var Q2;
            Q2=sQuery(id+"F43.wireOp",VERTEX,"E42.filletArc.start");
            cPlane(context, id + "F46", {"entities" : qUnion([Q0, Q1, Q2]), "cplaneType" : CPlaneType.THREE_POINT, "offset" : 25.4 * mm, "width" : 152.4 * mm, "height" : 152.4 * mm});
        }
        {
            var Q0;
            Q0=makeQuery(id+"F25.opExtrude","CAP_FACE",FACE,{"disambiguationData":[OSD([sQuery(id+"F24.wireOp",EDGE,"E30.bottom"),sQuery(id+"F24.wireOp",EDGE,"E30.top"),sQuery(id+"F24.wireOp",EDGE,"E30.left"),sQuery(id+"F24.wireOp",EDGE,"E30.right")])],"isStart":false});
            var sketch = newSketch(context, id + "F47", { "sketchPlane" : qUnion([Q0])});
            skCircle(sketch, "E46", {"center": v(-411.82, 635) * mm, "radius": 12.7 * mm});
            skSolve(sketch);
        }
        {
            var Q0;
            Q0=qCreatedBy(id+"F46.planeOp",FACE);
            var sketch = newSketch(context, id + "F48", { "sketchPlane" : qUnion([Q0])});
            skLineSegment(sketch, "E47", {"start": v(411.82, 787.4) * mm, "end": v(-7.28, 787.4) * mm});
            skSolve(sketch);
        }
        {
            var Q0;
            Q0=makeQuery(id+"F47.imprint","IMPRINT",FACE,{"disambiguationData":[TD([[makeQuery(id+"F47.imprint","IMPRINT",EDGE,{"derivedFrom":sQuery(id+"F47.wireOp",EDGE,"E46")}),1.0]])]});
            var Q1;
            Q1=sQuery(id+"F45.wireOp",EDGE,"E43");
            var Q2;
            Q2=sQuery(id+"F45.wireOp",EDGE,"E45.filletArc");
            var Q3;
            Q3=sQuery(id+"F45.wireOp",EDGE,"E44");
            var Q4;
            Q4=sQuery(id+"F48.wireOp",EDGE,"E47");
            var Q5;
            Q5=sQuery(id+"F43.wireOp",EDGE,"E41");
            var Q6;
            Q6=sQuery(id+"F43.wireOp",EDGE,"E42.filletArc");
            var Q7;
            Q7=sQuery(id+"F43.wireOp",EDGE,"E40");
            sweep(context, id + "F49", {"profiles" : qUnion([Q0]), "path" : qUnion([Q1, Q2, Q3, Q4, Q5, Q6, Q7])});
        }
        {
            var Q0;
            Q0=makeQuery(id+"F35.opExtrude","SWEPT_FACE",FACE,{"disambiguationData":[OSD([sQuery(id+"F34.wireOp",EDGE,"E37.left")])]});
            var sketch = newSketch(context, id + "F50", { "sketchPlane" : qUnion([Q0])});
            skLineSegment(sketch, "E48.bottom", {"start": v(2.17, 736.6) * mm, "end": v(497.47, 736.6) * mm});
            skLineSegment(sketch, "E48.top", {"start": v(2.17, 508) * mm, "end": v(497.47, 508) * mm});
            skLineSegment(sketch, "E48.left", {"start": v(2.17, 736.6) * mm, "end": v(2.17, 508) * mm});
            skLineSegment(sketch, "E48.right", {"start": v(497.47, 736.6) * mm, "end": v(497.47, 508) * mm});
            skSolve(sketch);
        }
        {
            var Q0;
            Q0=makeQuery(id+"F50.imprint","IMPRINT",FACE,{"disambiguationData":[TD([[makeQuery(id+"F50.imprint","IMPRINT",EDGE,{"derivedFrom":sQuery(id+"F50.wireOp",EDGE,"E48.bottom")}),-1.0]])]});
            var Q1;
            Q1=makeQuery(id+"F40.boolean.opBoolean","MERGE",FACE,{"derivedFrom":[makeQuery(id+"F39.opExtrude","CAP_FACE",FACE,{"disambiguationData":[OSD([sQuery(id+"F37.wireOp",EDGE,"E38.bottom"),sQuery(id+"F37.wireOp",EDGE,"E38.top"),sQuery(id+"F37.wireOp",EDGE,"E38.left"),sQuery(id+"F37.wireOp",EDGE,"E38.right")])],"isStart":true}),makeQuery(id+"F40.opExtrude","CAP_FACE",FACE,{"disambiguationData":[OSD([sQuery(id+"F38.wireOp",EDGE,"E39.bottom"),sQuery(id+"F38.wireOp",EDGE,"E39.top"),sQuery(id+"F38.wireOp",EDGE,"E39.left"),sQuery(id+"F38.wireOp",EDGE,"E39.right")])],"isStart":true})]});
            extrude(context, id + "F51", {"entities" : qUnion([Q0]), "endBound" : BoundingType.UP_TO_SURFACE, "oppositeDirection" : true, "endBoundEntityFace" : qUnion([Q1]), "depth" : 25.4 * mm});
        }
        {
            var Q0;
            Q0=makeQuery(id+"F51.opExtrude","SWEPT_FACE",FACE,{"disambiguationData":[OSD([sQuery(id+"F50.wireOp",EDGE,"E48.bottom")])]});
            shell(context, id + "F52", {"entities" : qUnion([Q0]), "thickness" : 12.7 * mm});
        }
        {
            var Q0;
            Q0=makeQuery(id+"F51.opExtrude","CAP_FACE",FACE,{"disambiguationData":[OSD([sQuery(id+"F50.wireOp",EDGE,"E48.bottom"),sQuery(id+"F50.wireOp",EDGE,"E48.top"),sQuery(id+"F50.wireOp",EDGE,"E48.left"),sQuery(id+"F50.wireOp",EDGE,"E48.right")])],"isStart":true});
            var sketch = newSketch(context, id + "F53", { "sketchPlane" : qUnion([Q0])});
            skLineSegment(sketch, "E49.bottom", {"start": v(-74.03, 736.6) * mm, "end": v(497.47, 736.6) * mm});
            skLineSegment(sketch, "E49.top", {"start": v(-74.03, 508) * mm, "end": v(497.47, 508) * mm});
            skLineSegment(sketch, "E49.left", {"start": v(-74.03, 736.6) * mm, "end": v(-74.03, 508) * mm});
            skLineSegment(sketch, "E49.right", {"start": v(497.47, 736.6) * mm, "end": v(497.47, 508) * mm});
            skSolve(sketch);
        }
        {
            var Q0;
            {var subQ2=sQuery(id+"F53.wireOp",EDGE,"E49.left");Q0=makeQuery(id+"F53.imprint","IMPRINT",FACE,{"disambiguationData":[TD([[makeQuery(id+"F53.imprint","IMPRINT",EDGE,{"derivedFrom":subQ2}),1.0]])]});}
            var Q1;
            {var subQ2=sQuery(id+"F53.wireOp",EDGE,"E49.right");Q1=makeQuery(id+"F53.imprint","IMPRINT",FACE,{"disambiguationData":[TD([[makeQuery(id+"F53.imprint","IMPRINT",EDGE,{"derivedFrom":subQ2}),-1.0]])]});}
            extrude(context, id + "F54", {"entities" : qUnion([Q0, Q1]), "depth" : 19.05 * mm});
        }
    });
